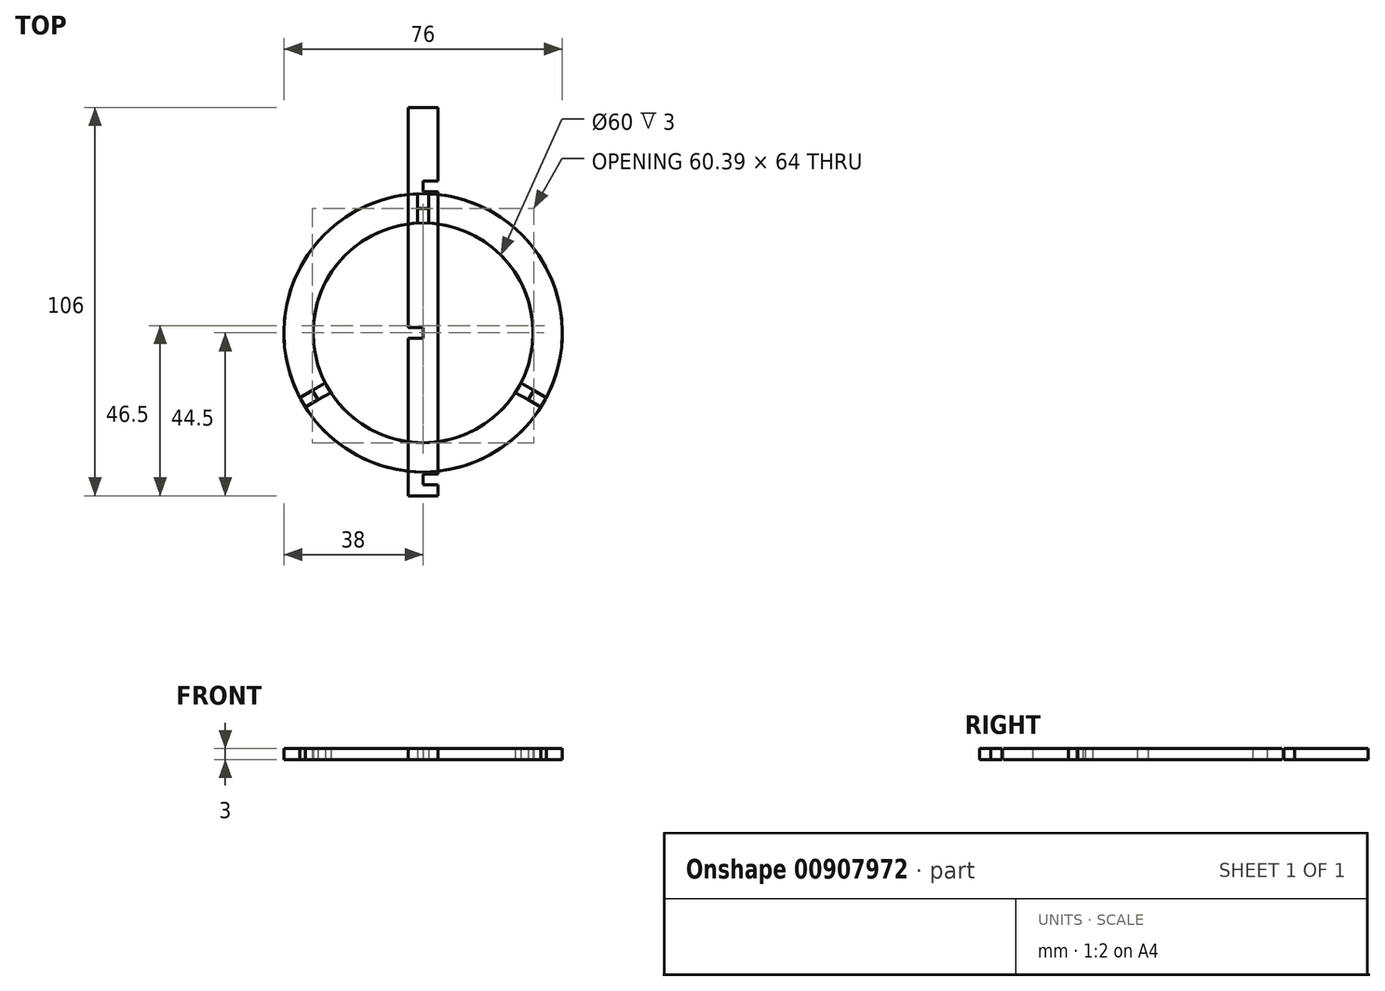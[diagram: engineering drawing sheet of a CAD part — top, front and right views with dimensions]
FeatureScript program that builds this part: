
annotation { "Feature Type Name" : "Feature", "Feature Type Description" : "" }
export const myFeature = defineFeature(function(context is Context, id is Id, definition is map)
    precondition{}
    {
        {
            assignVariable(context, id + "F0", {"name" : "material_thickness", "anyValue" : 3 * mm});
        }
        {
            var Q0;
            Q0=qCreatedBy(makeId("Top.planeOp"),FACE);
            var sketch = newSketch(context, id + "F1", { "sketchPlane" : qUnion([Q0])});
            skCircle(sketch, "E0", {"center": v(0, 0) * mm, "radius": 30 * mm, "construction": true});
            skLineSegment(sketch, "E1", {"start": v(-1.5, 37.97) * mm, "end": v(-1.5, 34) * mm});
            skLineSegment(sketch, "E2", {"start": v(-1.5, 34) * mm, "end": v(1.5, 34) * mm});
            skLineSegment(sketch, "E3", {"start": v(1.5, 34) * mm, "end": v(1.5, 37.97) * mm});
            skPoint(sketch, "E4", {"position": v(0, 34) * mm});
            skLineSegment(sketch, "E5.1.0", {"start": v(-30.2, -15.7) * mm, "end": v(-33.63, -17.69) * mm});
            skLineSegment(sketch, "E5.1.1", {"start": v(-32.13, -20.28) * mm, "end": v(-28.7, -18.3) * mm});
            skLineSegment(sketch, "E5.1.2", {"start": v(-28.7, -18.3) * mm, "end": v(-30.2, -15.7) * mm});
            skLineSegment(sketch, "E5.2.0", {"start": v(28.7, -18.3) * mm, "end": v(32.13, -20.28) * mm});
            skLineSegment(sketch, "E5.2.1", {"start": v(33.63, -17.69) * mm, "end": v(30.2, -15.7) * mm});
            skLineSegment(sketch, "E5.2.2", {"start": v(30.2, -15.7) * mm, "end": v(28.7, -18.3) * mm});
            skArc(sketch, "E6", {"start": v(-33.63, -17.69) * mm, "mid": v(-32.9, 19) * mm, "end": v(-1.5, 37.97) * mm});
            skArc(sketch, "E7", {"start": v(1.5, 37.97) * mm, "mid": v(32.9, 19) * mm, "end": v(33.63, -17.69) * mm});
            skArc(sketch, "E8", {"start": v(32.13, -20.28) * mm, "mid": v(0, -38) * mm, "end": v(-32.13, -20.28) * mm});
            skLineSegment(sketch, "E9", {"start": v(0, 38) * mm, "end": v(0, 30) * mm, "construction": true});
            skSolve(sketch);
        }
        {
            var Q0;
            Q0 = qSketchRegion(id + "F1", true);
            extrude(context, id + "F2", {"entities" : qUnion([Q0]), "depth" : getVariable(context, 'material_thickness'), "offsetDistance" : 25 * mm});
        }
        {
            var Q0;
            Q0=qCreatedBy(makeId("Top.planeOp"),FACE);
            var sketch = newSketch(context, id + "F3", { "sketchPlane" : qUnion([Q0])});
            skLineSegment(sketch, "E10", {"start": v(4, -44.5) * mm, "end": v(4, -41.5) * mm});
            skLineSegment(sketch, "E11", {"start": v(4, -41.5) * mm, "end": v(0, -41.5) * mm});
            skLineSegment(sketch, "E12", {"start": v(0, -41.5) * mm, "end": v(0, -38.5) * mm});
            skLineSegment(sketch, "E13", {"start": v(0, -38.5) * mm, "end": v(4, -38.5) * mm});
            skLineSegment(sketch, "E14", {"start": v(4, -38.5) * mm, "end": v(4, 38.5) * mm});
            skLineSegment(sketch, "E15", {"start": v(4, 38.5) * mm, "end": v(0, 38.5) * mm});
            skLineSegment(sketch, "E16", {"start": v(0, 38.5) * mm, "end": v(0, 41.5) * mm});
            skLineSegment(sketch, "E17", {"start": v(0, 41.5) * mm, "end": v(4, 41.5) * mm});
            skLineSegment(sketch, "E18", {"start": v(4, 41.5) * mm, "end": v(4, 61.5) * mm});
            skLineSegment(sketch, "E19", {"start": v(4, 61.5) * mm, "end": v(-4, 61.5) * mm});
            skLineSegment(sketch, "E20", {"start": v(-4, -44.5) * mm, "end": v(4, -44.5) * mm});
            skPoint(sketch, "E21", {"position": v(0, 61.5) * mm});
            skLineSegment(sketch, "E22", {"start": v(-4, -44.5) * mm, "end": v(-4, -1.5) * mm});
            skLineSegment(sketch, "E23", {"start": v(-4, -1.5) * mm, "end": v(0, -1.5) * mm});
            skLineSegment(sketch, "E24", {"start": v(0, -1.5) * mm, "end": v(0, 1.5) * mm});
            skLineSegment(sketch, "E25", {"start": v(0, 1.5) * mm, "end": v(-4, 1.5) * mm});
            skLineSegment(sketch, "E26", {"start": v(-4, 1.5) * mm, "end": v(-4, 61.5) * mm});
            skPoint(sketch, "E27", {"position": v(4, 0) * mm});
            skSolve(sketch);
        }
        {
            var Q0;
            Q0 = qSketchRegion(id + "F3", true);
            extrude(context, id + "F4", {"entities" : qUnion([Q0]), "depth" : getVariable(context, 'material_thickness'), "offsetDistance" : 25 * mm});
        }
        {
            var Q0;
            Q0=qCreatedBy(makeId("Top.planeOp"),FACE);
            var sketch = newSketch(context, id + "F5", { "sketchPlane" : qUnion([Q0])});
            skCircle(sketch, "E28", {"center": v(0, 0) * mm, "radius": 30 * mm, "construction": true});
            skPoint(sketch, "E29", {"position": v(0, 34) * mm});
            skLineSegment(sketch, "E30", {"start": v(0, 38) * mm, "end": v(0, 30) * mm, "construction": true});
            skCircle(sketch, "E31", {"center": v(0, 0) * mm, "radius": 38 * mm});
            skLineSegment(sketch, "E32", {"start": v(-1.5, 29.96) * mm, "end": v(-1.5, 34) * mm});
            skLineSegment(sketch, "E33", {"start": v(-1.5, 34) * mm, "end": v(1.5, 34) * mm});
            skLineSegment(sketch, "E34", {"start": v(1.5, 34) * mm, "end": v(1.5, 29.96) * mm});
            skLineSegment(sketch, "E35.1.0", {"start": v(26.7, -13.68) * mm, "end": v(30.2, -15.7) * mm});
            skLineSegment(sketch, "E35.1.1", {"start": v(30.2, -15.7) * mm, "end": v(28.7, -18.3) * mm});
            skLineSegment(sketch, "E35.1.2", {"start": v(28.7, -18.3) * mm, "end": v(25.2, -16.28) * mm});
            skLineSegment(sketch, "E35.2.0", {"start": v(-25.2, -16.28) * mm, "end": v(-28.7, -18.3) * mm});
            skLineSegment(sketch, "E35.2.1", {"start": v(-28.7, -18.3) * mm, "end": v(-30.2, -15.7) * mm});
            skLineSegment(sketch, "E35.2.2", {"start": v(-30.2, -15.7) * mm, "end": v(-26.7, -13.68) * mm});
            skLineSegment(sketch, "E35.anchor1", {"start": v(0, 0) * mm, "end": v(-1.5, 29.96) * mm, "construction": true});
            skLineSegment(sketch, "E35.anchor2", {"start": v(0, 0) * mm, "end": v(-25.2, -16.28) * mm, "construction": true});
            skArc(sketch, "E36", {"start": v(-1.5, 29.96) * mm, "mid": v(-25.98, 15) * mm, "end": v(-26.7, -13.68) * mm});
            skArc(sketch, "E37", {"start": v(1.5, 29.96) * mm, "mid": v(25.98, 15) * mm, "end": v(26.7, -13.68) * mm});
            skArc(sketch, "E38", {"start": v(-25.2, -16.28) * mm, "mid": v(0, -30) * mm, "end": v(25.2, -16.28) * mm});
            skSolve(sketch);
        }
        {
            var Q0;
            Q0 = qSketchRegion(id + "F5", true);
            extrude(context, id + "F6", {"entities" : qUnion([Q0]), "depth" : getVariable(context, 'material_thickness'), "offsetDistance" : 25 * mm});
        }
        {
            var Q0;
            Q0=qCreatedBy(makeId("Top.planeOp"),FACE);
            var sketch = newSketch(context, id + "F7", { "sketchPlane" : qUnion([Q0])});
            skCircle(sketch, "E39", {"center": v(0, 0) * mm, "radius": 30 * mm});
            skLineSegment(sketch, "E40", {"start": v(-1.5, 37.97) * mm, "end": v(-1.5, 34) * mm});
            skLineSegment(sketch, "E41", {"start": v(-1.5, 34) * mm, "end": v(1.5, 34) * mm});
            skLineSegment(sketch, "E42", {"start": v(1.5, 34) * mm, "end": v(1.5, 37.97) * mm});
            skPoint(sketch, "E43", {"position": v(0, 34) * mm});
            skLineSegment(sketch, "E44.1.0", {"start": v(-30.2, -15.7) * mm, "end": v(-33.63, -17.69) * mm});
            skLineSegment(sketch, "E44.1.1", {"start": v(-32.13, -20.28) * mm, "end": v(-28.7, -18.3) * mm});
            skLineSegment(sketch, "E44.1.2", {"start": v(-28.7, -18.3) * mm, "end": v(-30.2, -15.7) * mm});
            skLineSegment(sketch, "E44.2.0", {"start": v(28.7, -18.3) * mm, "end": v(32.13, -20.28) * mm});
            skLineSegment(sketch, "E44.2.1", {"start": v(33.63, -17.69) * mm, "end": v(30.2, -15.7) * mm});
            skLineSegment(sketch, "E44.2.2", {"start": v(30.2, -15.7) * mm, "end": v(28.7, -18.3) * mm});
            skArc(sketch, "E45", {"start": v(-33.63, -17.69) * mm, "mid": v(-32.9, 19) * mm, "end": v(-1.5, 37.97) * mm});
            skArc(sketch, "E46", {"start": v(1.5, 37.97) * mm, "mid": v(32.9, 19) * mm, "end": v(33.63, -17.69) * mm});
            skArc(sketch, "E47", {"start": v(32.13, -20.28) * mm, "mid": v(0, -38) * mm, "end": v(-32.13, -20.28) * mm});
            skLineSegment(sketch, "E48", {"start": v(0, 38) * mm, "end": v(0, 30) * mm, "construction": true});
            skSolve(sketch);
        }
        {
            var Q0;
            Q0 = qSketchRegion(id + "F7", true);
            extrude(context, id + "F8", {"entities" : qUnion([Q0]), "depth" : getVariable(context, 'material_thickness'), "offsetDistance" : 25 * mm});
        }
    });
